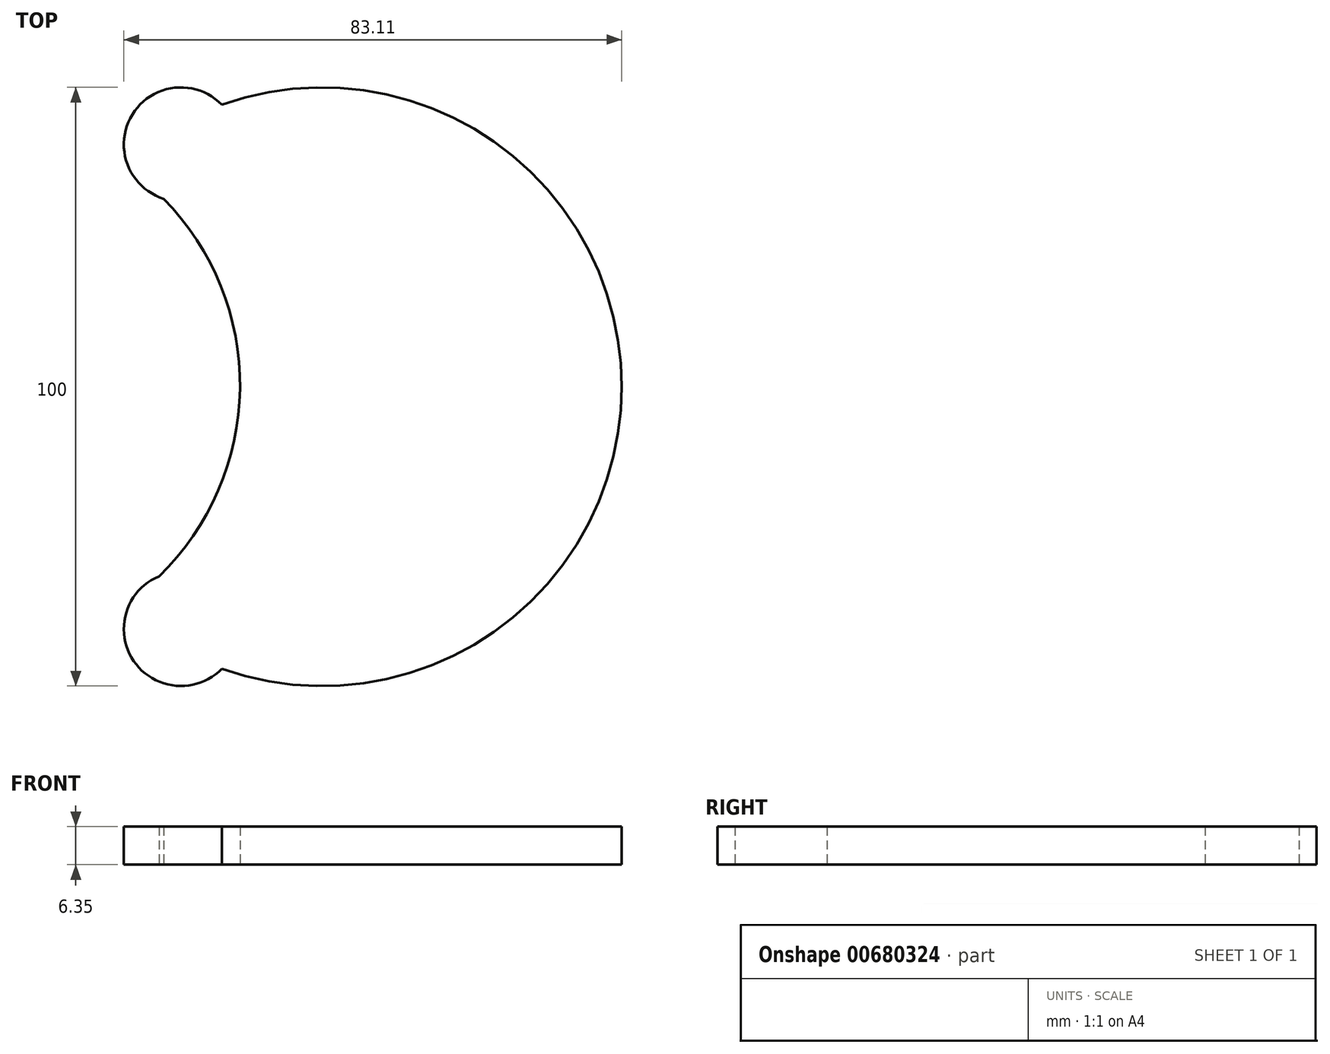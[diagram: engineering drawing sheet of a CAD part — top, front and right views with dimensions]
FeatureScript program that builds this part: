
annotation { "Feature Type Name" : "Feature", "Feature Type Description" : "" }
export const myFeature = defineFeature(function(context is Context, id is Id, definition is map)
    precondition{}
    {
        {
            var Q0;
            Q0=qCreatedBy(makeId("Top.planeOp"),FACE);
            var sketch = newSketch(context, id + "F0", { "sketchPlane" : qUnion([Q0])});
            skLineSegment(sketch, "E0.top", {"start": v(25, -50) * mm, "end": v(-25, -50) * mm});
            skLineSegment(sketch, "E0.right", {"start": v(-25, 50) * mm, "end": v(-25, -50) * mm});
            skArc(sketch, "E1", {"start": v(-24.65, -36.22) * mm, "mid": v(-24.1, -35.83) * mm, "end": v(-23.56, -35.43) * mm});
            skArc(sketch, "E2", {"start": v(-20.2, 48.75) * mm, "mid": v(-21.26, 49.39) * mm, "end": v(-22.33, 50) * mm});
            skArc(sketch, "E3", {"start": v(-8.64, 47.11) * mm, "mid": v(-23.58, 45.47) * mm, "end": v(-18.33, 31.39) * mm});
            skArc(sketch, "E4", {"start": v(-19.14, -31.68) * mm, "mid": v(-20.62, -48.5) * mm, "end": v(-5.96, -40.13) * mm});
            skLineSegment(sketch, "E5.bottom", {"start": v(-25, -50) * mm, "end": v(33.87, -50) * mm});
            skLineSegment(sketch, "E5.left", {"start": v(-25, -50) * mm, "end": v(-25, 50) * mm});
            skArc(sketch, "E6.trimOffspring", {"start": v(-8.24, -44.3) * mm, "mid": v(-8.45, -45.7) * mm, "end": v(-8.64, -47.11) * mm});
            skArc(sketch, "E7.trimOffspring", {"start": v(-19.14, -31.68) * mm, "mid": v(-5.6, -0.32) * mm, "end": v(-18.33, 31.39) * mm});
            skArc(sketch, "E8.trimOffspring", {"start": v(-24.03, 36.3) * mm, "mid": v(-24.34, 36.51) * mm, "end": v(-24.65, 36.73) * mm});
            skArc(sketch, "E9.trimOffspring", {"start": v(-23.26, -50) * mm, "mid": v(-21.93, -49.27) * mm, "end": v(-20.61, -48.5) * mm});
            skArc(sketch, "E10.trimOffspring", {"start": v(33.87, -50) * mm, "mid": v(33, -49.44) * mm, "end": v(32.16, -48.87) * mm});
            skPoint(sketch, "E11.right.end.orphan", {"position": v(75, 40.48) * mm});
            skLineSegment(sketch, "E12.bottom", {"start": v(46.3, -50) * mm, "end": v(75, -50) * mm});
            skLineSegment(sketch, "E13.bottom", {"start": v(-25, 50) * mm, "end": v(75, 50) * mm});
            skLineSegment(sketch, "E13.top", {"start": v(-25, -50) * mm, "end": v(75, -50) * mm});
            skLineSegment(sketch, "E13.right", {"start": v(75, 50) * mm, "end": v(75, -50) * mm});
            skArc(sketch, "E14", {"start": v(-8.64, -47.11) * mm, "mid": v(58.1, 0) * mm, "end": v(-8.64, 47.11) * mm});
            skSolve(sketch);
        }
        {
            var Q0;
            {var subQ0=sQuery(id+"F0.wireOp",EDGE,"Is2v1fQ1-ZBdX-rS4F-4GLm-UVHbrbp50TI0");var subQ1=makeQuery(id+"F0.imprint","INTERSECT",VERTEX,{"derivedFrom":[sQuery(id+"F0.wireOp",EDGE,"E0.bottom"),subQ0]});Q0=makeQuery(id+"F0.imprint","IMPRINT",FACE,{"disambiguationData":[TD([[makeQuery(id+"F0.imprint","IMPRINT",EDGE,{"disambiguationData":[TD([[subQ1,1.0]])],"derivedFrom":subQ0}),1.0]])]});}
            var Q1;
            {var subQ0=sQuery(id+"F0.wireOp",EDGE,"E1");var subQ1=sQuery(id+"F0.wireOp",EDGE,"Is2v1fQ1-ZBdX-rS4F-4GLm-UVHbrbp50TI0");var subQ5=makeQuery(id+"F0.imprint","INTERSECT",VERTEX,{"derivedFrom":[subQ1,subQ0]});Q1=makeQuery(id+"F0.imprint","IMPRINT",FACE,{"disambiguationData":[TD([[makeQuery(id+"F0.imprint","IMPRINT",EDGE,{"disambiguationData":[TD([[subQ5,-1.0]])],"derivedFrom":subQ1}),1.0]])]});}
            var Q2;
            {var subQ0=sQuery(id+"F0.wireOp",EDGE,"E1");var subQ1=sQuery(id+"F0.wireOp",EDGE,"Is2v1fQ1-ZBdX-rS4F-4GLm-UVHbrbp50TI0");var subQ3=makeQuery(id+"F0.imprint","INTERSECT",VERTEX,{"derivedFrom":[subQ1,subQ0]});Q2=makeQuery(id+"F0.imprint","IMPRINT",FACE,{"disambiguationData":[TD([[makeQuery(id+"F0.imprint","IMPRINT",EDGE,{"disambiguationData":[TD([[subQ3,1.0]])],"derivedFrom":subQ1}),1.0]])]});}
            var Q3;
            {var subQ5=sQuery(id+"F0.wireOp",EDGE,"E2");var subQ7=sQuery(id+"F0.wireOp",EDGE,"XaBmKFI2-PjV7-9AEn-iA4E-hYCk1PTkm2ty");var subQ8=makeQuery(id+"F0.imprint","INTERSECT",VERTEX,{"disambiguationData":[OD(0.0)],"derivedFrom":[subQ7,subQ5]});Q3=makeQuery(id+"F0.imprint","IMPRINT",FACE,{"disambiguationData":[TD([[makeQuery(id+"F0.imprint","IMPRINT",EDGE,{"disambiguationData":[TD([[subQ8,-1.0]])],"derivedFrom":subQ7}),-1.0]])]});}
            var Q4;
            {var subQ0=sQuery(id+"F0.wireOp",EDGE,"E2");var subQ1=sQuery(id+"F0.wireOp",EDGE,"XaBmKFI2-PjV7-9AEn-iA4E-hYCk1PTkm2ty");var subQ2=makeQuery(id+"F0.imprint","INTERSECT",VERTEX,{"disambiguationData":[OD(0.0)],"derivedFrom":[subQ1,subQ0]});Q4=makeQuery(id+"F0.imprint","IMPRINT",FACE,{"disambiguationData":[TD([[makeQuery(id+"F0.imprint","IMPRINT",EDGE,{"disambiguationData":[TD([[subQ2,-1.0]])],"derivedFrom":subQ1}),1.0]])]});}
            var Q5;
            {var subQ0=sQuery(id+"F0.wireOp",EDGE,"E2");var subQ1=sQuery(id+"F0.wireOp",EDGE,"1AJWMQxB-zm41-oJMR-8iGR-Tk6yRRpPPpZ8");var subQ2=makeQuery(id+"F0.imprint","INTERSECT",VERTEX,{"disambiguationData":[OD(0.0)],"derivedFrom":[subQ1,subQ0]});Q5=makeQuery(id+"F0.imprint","IMPRINT",FACE,{"disambiguationData":[TD([[makeQuery(id+"F0.imprint","IMPRINT",EDGE,{"disambiguationData":[TD([[subQ2,-1.0]])],"derivedFrom":subQ1}),1.0]])]});}
            var Q6;
            {var subQ0=sQuery(id+"F0.wireOp",EDGE,"E1");var subQ1=sQuery(id+"F0.wireOp",EDGE,"1AJWMQxB-zm41-oJMR-8iGR-Tk6yRRpPPpZ8");var subQ3=makeQuery(id+"F0.imprint","INTERSECT",VERTEX,{"derivedFrom":[subQ1,subQ0]});Q6=makeQuery(id+"F0.imprint","IMPRINT",FACE,{"disambiguationData":[TD([[makeQuery(id+"F0.imprint","IMPRINT",EDGE,{"disambiguationData":[TD([[subQ3,-1.0]])],"derivedFrom":subQ1}),1.0]])]});}
            var Q7;
            {var subQ0=sQuery(id+"F0.wireOp",EDGE,"1AJWMQxB-zm41-oJMR-8iGR-Tk6yRRpPPpZ8");var subQ1=makeQuery(id+"F0.imprint","INTERSECT",VERTEX,{"derivedFrom":[sQuery(id+"F0.wireOp",EDGE,"XaBmKFI2-PjV7-9AEn-iA4E-hYCk1PTkm2ty"),subQ0]});Q7=makeQuery(id+"F0.imprint","IMPRINT",FACE,{"disambiguationData":[TD([[makeQuery(id+"F0.imprint","IMPRINT",EDGE,{"disambiguationData":[TD([[subQ1,-1.0]])],"derivedFrom":subQ0}),1.0]])]});}
            var Q8;
            {var subQ0=sQuery(id+"F0.wireOp",EDGE,"E4");var subQ1=sQuery(id+"F0.wireOp",EDGE,"E1");var subQ7=makeQuery(id+"F0.imprint","INTERSECT",VERTEX,{"disambiguationData":[OD(0.0)],"derivedFrom":[subQ1,subQ0]});Q8=makeQuery(id+"F0.imprint","IMPRINT",FACE,{"disambiguationData":[TD([[makeQuery(id+"F0.imprint","IMPRINT",EDGE,{"disambiguationData":[TD([[subQ7,-1.0]])],"derivedFrom":subQ1}),-1.0]])]});}
            var Q9;
            {var subQ0=sQuery(id+"F0.wireOp",EDGE,"E4");var subQ1=sQuery(id+"F0.wireOp",EDGE,"E1");var subQ2=makeQuery(id+"F0.imprint","INTERSECT",VERTEX,{"disambiguationData":[OD(0.0)],"derivedFrom":[subQ1,subQ0]});Q9=makeQuery(id+"F0.imprint","IMPRINT",FACE,{"disambiguationData":[TD([[makeQuery(id+"F0.imprint","IMPRINT",EDGE,{"disambiguationData":[TD([[subQ2,-1.0]])],"derivedFrom":subQ1}),1.0]])]});}
            var Q10;
            {var subQ0=sQuery(id+"F0.wireOp",EDGE,"E4");var subQ1=sQuery(id+"F0.wireOp",EDGE,"E1");var subQ2=makeQuery(id+"F0.imprint","INTERSECT",VERTEX,{"disambiguationData":[OD(1.0)],"derivedFrom":[subQ1,subQ0]});Q10=makeQuery(id+"F0.imprint","IMPRINT",FACE,{"disambiguationData":[TD([[makeQuery(id+"F0.imprint","IMPRINT",EDGE,{"disambiguationData":[TD([[subQ2,-1.0]])],"derivedFrom":subQ1}),-1.0]])]});}
            var Q11;
            {var subQ0=sQuery(id+"F0.wireOp",EDGE,"E3");var subQ4=makeQuery(id+"F0.imprint","INTERSECT",VERTEX,{"derivedFrom":[subQ0,sQuery(id+"F0.wireOp",EDGE,"E5.top")]});Q11=makeQuery(id+"F0.imprint","IMPRINT",FACE,{"disambiguationData":[TD([[makeQuery(id+"F0.imprint","IMPRINT",EDGE,{"disambiguationData":[TD([[subQ4,-1.0]])],"derivedFrom":subQ0}),1.0]])]});}
            var Q12;
            {var subQ0=sQuery(id+"F0.wireOp",EDGE,"E4");var subQ4=makeQuery(id+"F0.imprint","INTERSECT",VERTEX,{"derivedFrom":[subQ0,sQuery(id+"F0.wireOp",EDGE,"E5.bottom")]});Q12=makeQuery(id+"F0.imprint","IMPRINT",FACE,{"disambiguationData":[TD([[makeQuery(id+"F0.imprint","IMPRINT",EDGE,{"disambiguationData":[TD([[subQ4,1.0]])],"derivedFrom":subQ0}),1.0]])]});}
            var Q13;
            {var subQ0=sQuery(id+"F0.wireOp",EDGE,"84e9ec3b-da6a-4109-a636-10c67649671f0.MirrorC");var subQ3=makeQuery(id+"F0.imprint","IMPRINT",VERTEX,{"derivedFrom":subQ0});Q13=makeQuery(id+"F0.imprint","IMPRINT",FACE,{"disambiguationData":[TD([[makeQuery(id+"F0.imprint","IMPRINT",EDGE,{"disambiguationData":[TD([[subQ3,1.0]])],"derivedFrom":subQ0}),-1.0]])]});}
            var Q14;
            {var subQ1=sQuery(id+"F0.wireOp",EDGE,"ff3cbf99-9e95-4a13-927f-f1e4663ae94f0.MirrorC");var subQ4=sQuery(id+"F0.wireOp",EDGE,"dbb5db56-5477-43c1-a154-d75ed721ab0c.trimOffspring");var subQ5=makeQuery(id+"F0.imprint","INTERSECT",VERTEX,{"derivedFrom":[subQ1,subQ4]});Q14=makeQuery(id+"F0.imprint","IMPRINT",FACE,{"disambiguationData":[TD([[makeQuery(id+"F0.imprint","IMPRINT",EDGE,{"disambiguationData":[TD([[subQ5,1.0]])],"derivedFrom":subQ1}),-1.0]])]});}
            var Q15;
            {var subQ6=sQuery(id+"F0.wireOp",EDGE,"274a91ff-d93d-49d6-a6e7-9a811cbac7e8.trimOffspring");Q15=makeQuery(id+"F0.imprint","IMPRINT",FACE,{"disambiguationData":[TD([[makeQuery(id+"F0.imprint","IMPRINT",EDGE,{"derivedFrom":subQ6}),-1.0]])]});}
            var Q16;
            {var subQ0=sQuery(id+"F0.wireOp",EDGE,"91dc7be7-ba82-4ac9-92d0-e31783462ea90.MirrorCS");var subQ1=sQuery(id+"F0.wireOp",EDGE,"dbb5db56-5477-43c1-a154-d75ed721ab0c.trimOffspring");var subQ2=makeQuery(id+"F0.imprint","INTERSECT",VERTEX,{"derivedFrom":[subQ1,subQ0]});Q16=makeQuery(id+"F0.imprint","IMPRINT",FACE,{"disambiguationData":[TD([[makeQuery(id+"F0.imprint","IMPRINT",EDGE,{"disambiguationData":[TD([[subQ2,-1.0]])],"derivedFrom":subQ1}),-1.0]])]});}
            var Q17;
            {var subQ3=sQuery(id+"F0.wireOp",EDGE,"E10.trimOffspring");Q17=makeQuery(id+"F0.imprint","IMPRINT",FACE,{"disambiguationData":[TD([[makeQuery(id+"F0.imprint","IMPRINT",EDGE,{"derivedFrom":subQ3}),1.0]])]});}
            var Q18;
            {var subQ3=sQuery(id+"F0.wireOp",EDGE,"274a91ff-d93d-49d6-a6e7-9a811cbac7e8.trimOffspring");Q18=makeQuery(id+"F0.imprint","IMPRINT",FACE,{"disambiguationData":[TD([[makeQuery(id+"F0.imprint","IMPRINT",EDGE,{"derivedFrom":subQ3}),1.0]])]});}
            var Q19;
            {var subQ0=sQuery(id+"F0.wireOp",EDGE,"b53edb47-2054-462a-a509-28436a7c45c1.trimOffspring");var subQ1=sQuery(id+"F0.wireOp",EDGE,"TklKttEs-CvJK-MCK4-x6ks-5O2dMt5gFvr1");var subQ2=makeQuery(id+"F0.imprint","INTERSECT",VERTEX,{"derivedFrom":[subQ1,subQ0]});Q19=makeQuery(id+"F0.imprint","IMPRINT",FACE,{"disambiguationData":[TD([[makeQuery(id+"F0.imprint","IMPRINT",EDGE,{"disambiguationData":[TD([[subQ2,1.0]])],"derivedFrom":subQ1}),1.0]])]});}
            var Q20;
            {var subQ0=sQuery(id+"F0.wireOp",EDGE,"kFnup37U-975r-R3gH-yhVY-lWQdXskkqw86");var subQ1=sQuery(id+"F0.wireOp",EDGE,"E0.left");var subQ2=makeQuery(id+"F0.imprint","INTERSECT",VERTEX,{"disambiguationData":[OD(1.0)],"derivedFrom":[subQ1,subQ0]});Q20=makeQuery(id+"F0.imprint","IMPRINT",FACE,{"disambiguationData":[TD([[makeQuery(id+"F0.imprint","IMPRINT",EDGE,{"disambiguationData":[TD([[subQ2,-1.0]])],"derivedFrom":subQ1}),1.0]])]});}
            var Q21;
            {var subQ0=sQuery(id+"F0.wireOp",EDGE,"ff3cbf99-9e95-4a13-927f-f1e4663ae94f0.MirrorC");var subQ1=sQuery(id+"F0.wireOp",EDGE,"E0.left");var subQ2=makeQuery(id+"F0.imprint","INTERSECT",VERTEX,{"derivedFrom":[subQ1,subQ0]});Q21=makeQuery(id+"F0.imprint","IMPRINT",FACE,{"disambiguationData":[TD([[makeQuery(id+"F0.imprint","IMPRINT",EDGE,{"disambiguationData":[TD([[subQ2,-1.0]])],"derivedFrom":subQ1}),1.0]])]});}
            var Q22;
            {var subQ6=sQuery(id+"F0.wireOp",EDGE,"E10.trimOffspring");Q22=makeQuery(id+"F0.imprint","IMPRINT",FACE,{"disambiguationData":[TD([[makeQuery(id+"F0.imprint","IMPRINT",EDGE,{"derivedFrom":subQ6}),-1.0]])]});}
            var Q23;
            {var subQ0=sQuery(id+"F0.wireOp",EDGE,"Zz2JqQw8-Ova1-09Ti-ANcW-KtaURACnHauL");Q23=makeQuery(id+"F0.imprint","IMPRINT",FACE,{"disambiguationData":[TD([[makeQuery(id+"F0.imprint","IMPRINT",EDGE,{"derivedFrom":subQ0}),1.0]])]});}
            extrude(context, id + "F1", {"entities" : qUnion([Q0, Q1, Q2, Q3, Q4, Q5, Q6, Q7, Q8, Q9, Q10, Q11, Q12, Q13, Q14, Q15, Q16, Q17, Q18, Q19, Q20, Q21, Q22, Q23]), "depth" : 6.35 * mm, "offsetDistance" : 25.4 * mm});
        }
    });
